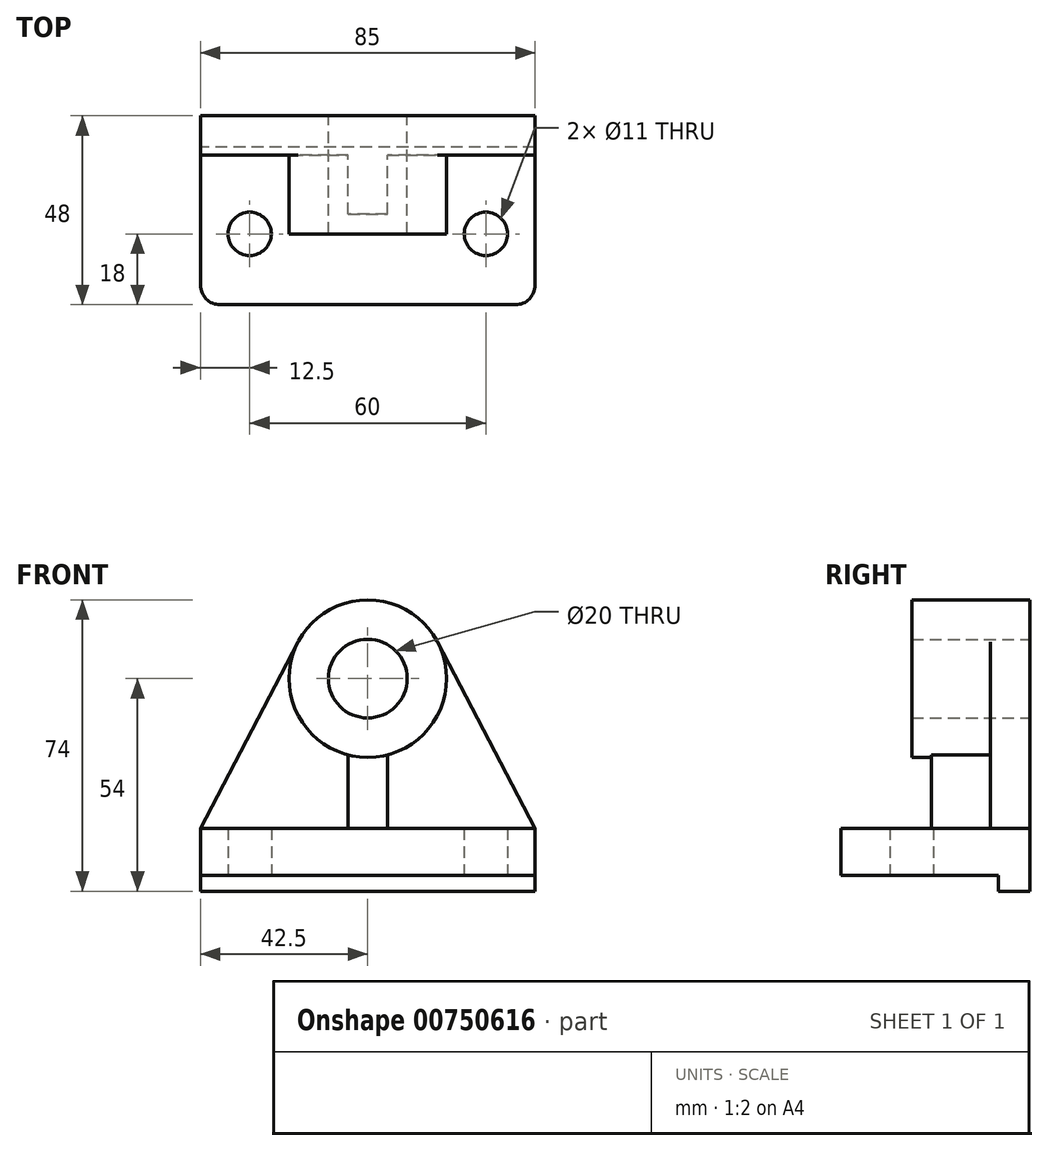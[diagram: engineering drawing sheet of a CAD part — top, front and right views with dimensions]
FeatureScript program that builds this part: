
annotation { "Feature Type Name" : "Feature", "Feature Type Description" : "" }
export const myFeature = defineFeature(function(context is Context, id is Id, definition is map)
    precondition{}
    {
        {
            var Q0;
            Q0=qCreatedBy(makeId("Top.planeOp"),FACE);
            var sketch = newSketch(context, id + "F0", { "sketchPlane" : qUnion([Q0])});
            skLineSegment(sketch, "E0.bottom", {"start": v(5, 0) * mm, "end": v(80, 0) * mm});
            skLineSegment(sketch, "E0.top", {"start": v(0, 48) * mm, "end": v(85, 48) * mm});
            skLineSegment(sketch, "E0.left", {"start": v(0, 5) * mm, "end": v(0, 48) * mm});
            skLineSegment(sketch, "E0.right", {"start": v(85, 5) * mm, "end": v(85, 48) * mm});
            skCircle(sketch, "E1", {"center": v(72.5, 18) * mm, "radius": 5.5 * mm});
            skCircle(sketch, "E2", {"center": v(12.5, 18) * mm, "radius": 5.5 * mm});
            skPoint(sketch, "E3.visualSharp", {"position": v(0, 0) * mm});
            skArc(sketch, "E3.filletArc", {"start": v(0, 5) * mm, "mid": v(1.46, 1.46) * mm, "end": v(5, 0) * mm});
            skPoint(sketch, "E4.visualSharp", {"position": v(85, 0) * mm});
            skArc(sketch, "E4.filletArc", {"start": v(80, 0) * mm, "mid": v(83.54, 1.46) * mm, "end": v(85, 5) * mm});
            skSolve(sketch);
        }
        {
            var Q0;
            Q0=makeQuery(id+"F0.imprint","IMPRINT",FACE,{"disambiguationData":[TD([[makeQuery(id+"F0.imprint","IMPRINT",EDGE,{"derivedFrom":sQuery(id+"F0.wireOp",EDGE,"E0.bottom")}),1.0]])]});
            extrude(context, id + "F1", {"entities" : qUnion([Q0]), "depth" : 12 * mm, "offsetDistance" : 25 * mm});
        }
        {
            var Q0;
            Q0=makeQuery(id+"F1.opExtrude","SWEPT_FACE",FACE,{"disambiguationData":[OSD([sQuery(id+"F0.wireOp",EDGE,"E0.left")])]});
            var sketch = newSketch(context, id + "F2", { "sketchPlane" : qUnion([Q0])});
            skLineSegment(sketch, "E5", {"start": v(-48, 0) * mm, "end": v(-40, 0) * mm});
            skLineSegment(sketch, "E6", {"start": v(-40, 0) * mm, "end": v(-40, -4) * mm});
            skLineSegment(sketch, "E7", {"start": v(-40, -4) * mm, "end": v(-48, -4) * mm});
            skLineSegment(sketch, "E8", {"start": v(-48, -4) * mm, "end": v(-48, 0) * mm});
            skSolve(sketch);
        }
        {
            var Q0;
            Q0=makeQuery(id+"F2.imprint","IMPRINT",FACE,{"disambiguationData":[TD([[makeQuery(id+"F2.imprint","IMPRINT",EDGE,{"derivedFrom":sQuery(id+"F2.wireOp",EDGE,"E5")}),1.0]])]});
            extrude(context, id + "F3", {"entities" : qUnion([Q0]), "operationType" : NewBodyOperationType.ADD, "oppositeDirection" : true, "depth" : 85 * mm, "offsetDistance" : 25 * mm});
        }
        {
            var Q0;
            Q0=makeQuery(id+"F3.boolean.opBoolean","MERGE",FACE,{"derivedFrom":[makeQuery(id+"F1.opExtrude","SWEPT_FACE",FACE,{"disambiguationData":[OSD([sQuery(id+"F0.wireOp",EDGE,"E0.top")])]}),makeQuery(id+"F3.opExtrude","SWEPT_FACE",FACE,{"disambiguationData":[OSD([sQuery(id+"F2.wireOp",EDGE,"E8")])]})]});
            var sketch = newSketch(context, id + "F4", { "sketchPlane" : qUnion([Q0])});
            skCircle(sketch, "E9", {"center": v(-42.5, 50) * mm, "radius": 10 * mm});
            skLineSegment(sketch, "E10", {"start": v(-85, 12) * mm, "end": v(-60.21, 59.29) * mm});
            skLineSegment(sketch, "E11", {"start": v(0, 12) * mm, "end": v(-24.79, 59.29) * mm});
            skArc(sketch, "E12", {"start": v(-24.79, 59.29) * mm, "mid": v(-42.5, 70) * mm, "end": v(-60.21, 59.29) * mm});
            skSolve(sketch);
        }
        {
            var Q0;
            Q0=makeQuery(id+"F4.imprint","IMPRINT",FACE,{"disambiguationData":[TD([[makeQuery(id+"F4.imprint","IMPRINT",EDGE,{"derivedFrom":sQuery(id+"F4.wireOp",EDGE,"E9")}),-1.0]])]});
            extrude(context, id + "F5", {"entities" : qUnion([Q0]), "operationType" : NewBodyOperationType.ADD, "oppositeDirection" : true, "depth" : 10 * mm, "offsetDistance" : 25 * mm});
        }
        {
            var Q0;
            Q0=makeQuery(id+"F5.opExtrude","CAP_FACE",FACE,{"disambiguationData":[OSD([sQuery(id+"F0.wireOp",EDGE,"E0.top"),sQuery(id+"F4.wireOp",EDGE,"E9"),sQuery(id+"F4.wireOp",EDGE,"E10"),sQuery(id+"F4.wireOp",EDGE,"E11"),sQuery(id+"F4.wireOp",EDGE,"E12")])],"isStart":false});
            var sketch = newSketch(context, id + "F6", { "sketchPlane" : qUnion([Q0])});
            skCircle(sketch, "E13", {"center": v(42.5, 50) * mm, "radius": 10 * mm});
            skCircle(sketch, "E14", {"center": v(42.5, 50) * mm, "radius": 20 * mm});
            skSolve(sketch);
        }
        {
            var Q0;
            Q0=makeQuery(id+"F6.imprint","IMPRINT",FACE,{"disambiguationData":[TD([[makeQuery(id+"F6.imprint","IMPRINT",EDGE,{"derivedFrom":sQuery(id+"F6.wireOp",EDGE,"E13")}),1.0]])]});
            extrude(context, id + "F7", {"entities" : qUnion([Q0]), "operationType" : NewBodyOperationType.ADD, "depth" : 20 * mm, "offsetDistance" : 25 * mm});
        }
        {
            var Q0;
            Q0=makeQuery(id+"F5.opExtrude","CAP_FACE",FACE,{"disambiguationData":[OSD([sQuery(id+"F0.wireOp",EDGE,"E0.top"),sQuery(id+"F4.wireOp",EDGE,"E9"),sQuery(id+"F4.wireOp",EDGE,"E10"),sQuery(id+"F4.wireOp",EDGE,"E11"),sQuery(id+"F4.wireOp",EDGE,"E12")])],"isStart":false});
            var sketch = newSketch(context, id + "F8", { "sketchPlane" : qUnion([Q0])});
            skLineSegment(sketch, "E15", {"start": v(42.5, 12) * mm, "end": v(47.5, 12) * mm});
            skLineSegment(sketch, "E16", {"start": v(47.5, 12) * mm, "end": v(47.5, 30.64) * mm});
            skLineSegment(sketch, "E17", {"start": v(42.5, 12) * mm, "end": v(37.5, 12) * mm});
            skLineSegment(sketch, "E18", {"start": v(37.5, 12) * mm, "end": v(37.5, 30.64) * mm});
            skArc(sketch, "E19", {"start": v(37.5, 30.64) * mm, "mid": v(42.5, 30) * mm, "end": v(47.5, 30.64) * mm});
            skSolve(sketch);
        }
        {
            var Q0;
            Q0=makeQuery(id+"F8.imprint","IMPRINT",FACE,{"disambiguationData":[TD([[makeQuery(id+"F8.imprint","IMPRINT",EDGE,{"derivedFrom":sQuery(id+"F8.wireOp",EDGE,"E15")}),1.0]])]});
            extrude(context, id + "F9", {"entities" : qUnion([Q0]), "operationType" : NewBodyOperationType.ADD, "depth" : 15 * mm, "offsetDistance" : 25 * mm});
        }
    });
